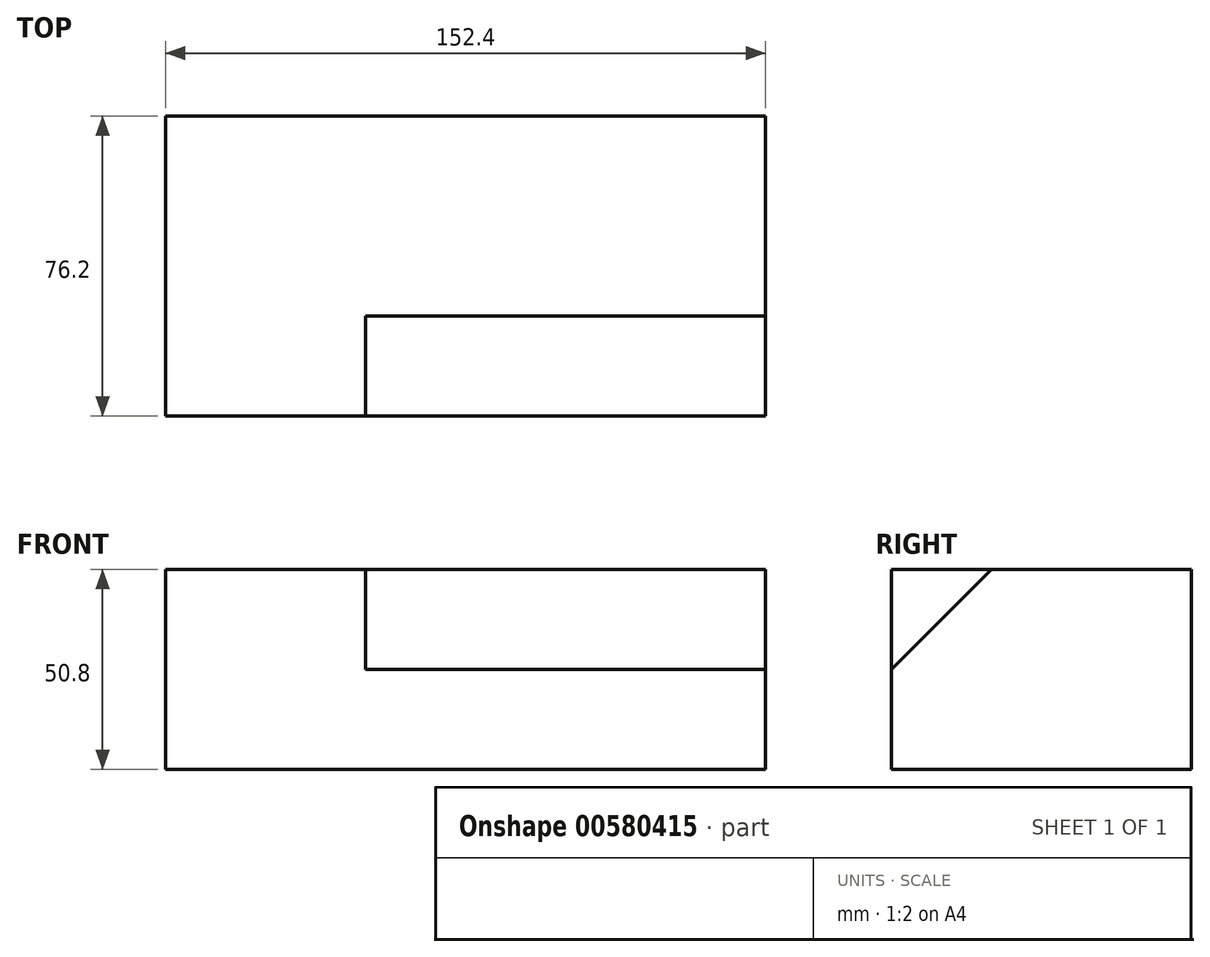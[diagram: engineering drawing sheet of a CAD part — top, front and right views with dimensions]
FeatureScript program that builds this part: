
annotation { "Feature Type Name" : "Feature", "Feature Type Description" : "" }
export const myFeature = defineFeature(function(context is Context, id is Id, definition is map)
    precondition{}
    {
        {
            var Q0;
            Q0=qCreatedBy(makeId("Right.planeOp"),FACE);
            var sketch = newSketch(context, id + "F0", { "sketchPlane" : qUnion([Q0])});
            skLineSegment(sketch, "E0", {"start": v(-27.18, 31.13) * mm, "end": v(49.02, 31.13) * mm});
            skLineSegment(sketch, "E1", {"start": v(49.02, 31.13) * mm, "end": v(49.02, -19.67) * mm});
            skLineSegment(sketch, "E2", {"start": v(49.02, -19.67) * mm, "end": v(-27.18, -19.67) * mm});
            skLineSegment(sketch, "E3", {"start": v(-27.18, -19.67) * mm, "end": v(-27.18, 31.13) * mm});
            skLineSegment(sketch, "E4", {"start": v(-1.78, 31.13) * mm, "end": v(-27.18, 5.73) * mm});
            skSolve(sketch);
        }
        {
            var Q0;
            {var subQ3=sQuery(id+"F0.wireOp",EDGE,"E4");Q0=makeQuery(id+"F0.imprint","IMPRINT",FACE,{"disambiguationData":[TD([[makeQuery(id+"F0.imprint","IMPRINT",EDGE,{"derivedFrom":subQ3}),-1.0]])]});}
            extrude(context, id + "F1", {"entities" : qUnion([Q0]), "depth" : 50.8 * mm, "offsetDistance" : 25.4 * mm});
        }
        {
            var Q0;
            {var subQ3=sQuery(id+"F0.wireOp",EDGE,"E1");Q0=makeQuery(id+"F0.imprint","IMPRINT",FACE,{"disambiguationData":[TD([[makeQuery(id+"F0.imprint","IMPRINT",EDGE,{"derivedFrom":subQ3}),-1.0]])]});}
            extrude(context, id + "F2", {"entities" : qUnion([Q0]), "operationType" : NewBodyOperationType.ADD, "depth" : 152.4 * mm, "offsetDistance" : 25.4 * mm});
        }
    });
